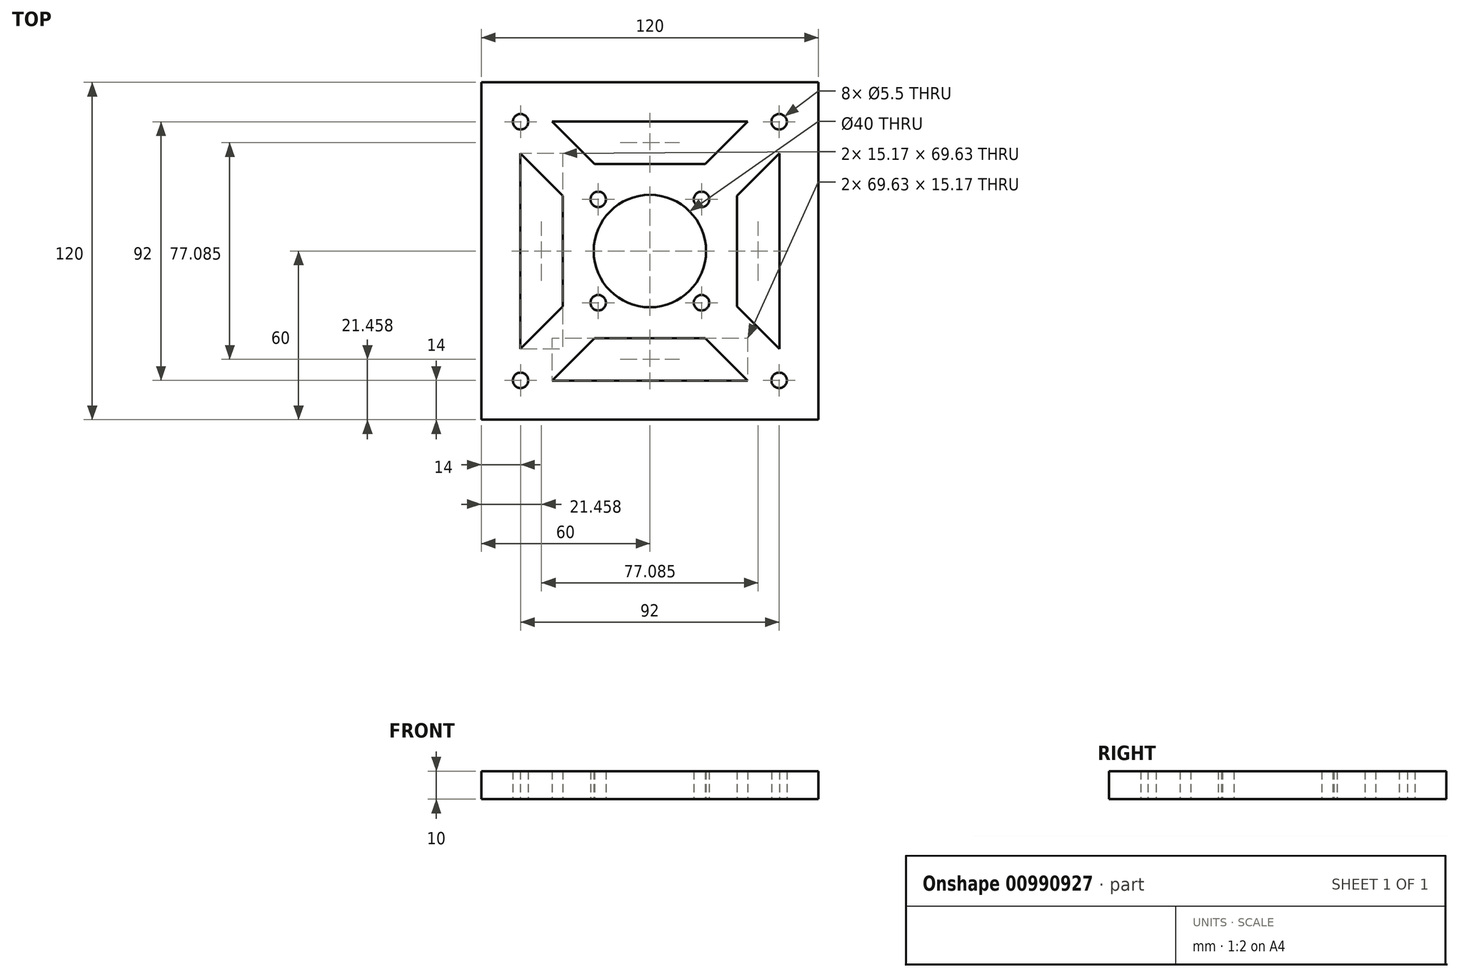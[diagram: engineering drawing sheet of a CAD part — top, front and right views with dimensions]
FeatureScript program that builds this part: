
annotation { "Feature Type Name" : "Feature", "Feature Type Description" : "" }
export const myFeature = defineFeature(function(context is Context, id is Id, definition is map)
    precondition{}
    {
        {
            var Q0;
            Q0=qCreatedBy(makeId("Top.planeOp"),FACE);
            var sketch = newSketch(context, id + "F0", { "sketchPlane" : qUnion([Q0])});
            skLineSegment(sketch, "E0.bottom", {"start": v(60, -60) * mm, "end": v(-60, -60) * mm});
            skLineSegment(sketch, "E0.top", {"start": v(60, 60) * mm, "end": v(-60, 60) * mm});
            skLineSegment(sketch, "E0.left", {"start": v(60, -60) * mm, "end": v(60, 60) * mm});
            skLineSegment(sketch, "E0.right", {"start": v(-60, -60) * mm, "end": v(-60, 60) * mm});
            skPoint(sketch, "E0.middle", {"position": v(0, 0) * mm});
            skCircle(sketch, "E1", {"center": v(0, 0) * mm, "radius": 20 * mm});
            skLineSegment(sketch, "E2", {"start": v(20, 0) * mm, "end": v(60, 0) * mm, "construction": true});
            skLineSegment(sketch, "E3", {"start": v(0, -20) * mm, "end": v(0, -60) * mm, "construction": true});
            skCircle(sketch, "E4", {"center": v(-46, 46) * mm, "radius": 2.75 * mm});
            skCircle(sketch, "E5.MirrorC", {"center": v(46, 46) * mm, "radius": 2.75 * mm});
            skCircle(sketch, "E6.MirrorC", {"center": v(-46, -46) * mm, "radius": 2.75 * mm});
            skCircle(sketch, "E7.MirrorC", {"center": v(46, -46) * mm, "radius": 2.75 * mm});
            skCircle(sketch, "E8", {"center": v(-18.38, 18.38) * mm, "radius": 2.75 * mm});
            skCircle(sketch, "E9.MirrorC", {"center": v(18.38, 18.38) * mm, "radius": 2.75 * mm});
            skCircle(sketch, "E10.MirrorC", {"center": v(-18.38, -18.38) * mm, "radius": 2.75 * mm});
            skCircle(sketch, "E11.MirrorC", {"center": v(18.38, -18.38) * mm, "radius": 2.75 * mm});
            skCircle(sketch, "E12", {"center": v(0, 0) * mm, "radius": 26 * mm, "construction": true});
            skLineSegment(sketch, "E13", {"start": v(-46, 46) * mm, "end": v(46, -46) * mm, "construction": true});
            skLineSegment(sketch, "E14", {"start": v(-46, -46) * mm, "end": v(46, 46) * mm, "construction": true});
            skLineSegment(sketch, "E15", {"start": v(-51.42, 40.11) * mm, "end": v(40.58, -51.89) * mm, "construction": true});
            skLineSegment(sketch, "E16.MirrorCS", {"start": v(-40.11, 51.42) * mm, "end": v(51.89, -40.58) * mm, "construction": true});
            skLineSegment(sketch, "E17.MirrorCS", {"start": v(40.11, 51.42) * mm, "end": v(-51.89, -40.58) * mm, "construction": true});
            skLineSegment(sketch, "E18.MirrorCS", {"start": v(51.42, 40.11) * mm, "end": v(-40.58, -51.89) * mm, "construction": true});
            skLineSegment(sketch, "E19", {"start": v(-30.96, 19.64) * mm, "end": v(-30.96, -19.64) * mm});
            skLineSegment(sketch, "E20.MirrorCS", {"start": v(19.64, -30.96) * mm, "end": v(-19.64, -30.96) * mm});
            skLineSegment(sketch, "E21.MirrorCS", {"start": v(46, -46) * mm, "end": v(-46, 46) * mm, "construction": true});
            skLineSegment(sketch, "E22.MirrorCS", {"start": v(-19.64, 30.96) * mm, "end": v(19.64, 30.96) * mm});
            skLineSegment(sketch, "E23.MirrorCS", {"start": v(30.96, 19.64) * mm, "end": v(30.96, -19.64) * mm});
            skLineSegment(sketch, "E24", {"start": v(-46.13, 34.81) * mm, "end": v(-46.13, -34.81) * mm});
            skLineSegment(sketch, "E25.MirrorCS", {"start": v(46.13, 34.81) * mm, "end": v(46.13, -34.81) * mm});
            skLineSegment(sketch, "E26.MirrorCS", {"start": v(-34.81, -46.13) * mm, "end": v(34.81, -46.13) * mm});
            skLineSegment(sketch, "E27.MirrorCS", {"start": v(-34.81, 46.13) * mm, "end": v(34.81, 46.13) * mm});
            skLineSegment(sketch, "E28", {"start": v(-46.13, 34.81) * mm, "end": v(-30.96, 19.64) * mm});
            skLineSegment(sketch, "E29", {"start": v(-30.96, -19.64) * mm, "end": v(-46.13, -34.81) * mm});
            skLineSegment(sketch, "E30", {"start": v(-34.81, -46.13) * mm, "end": v(-19.64, -30.96) * mm});
            skLineSegment(sketch, "E31", {"start": v(19.64, -30.96) * mm, "end": v(34.81, -46.13) * mm});
            skLineSegment(sketch, "E32", {"start": v(46.13, -34.81) * mm, "end": v(30.96, -19.64) * mm});
            skLineSegment(sketch, "E33", {"start": v(30.96, 19.64) * mm, "end": v(46.13, 34.81) * mm});
            skLineSegment(sketch, "E34", {"start": v(34.81, 46.13) * mm, "end": v(19.64, 30.96) * mm});
            skLineSegment(sketch, "E35", {"start": v(-19.64, 30.96) * mm, "end": v(-34.81, 46.13) * mm});
            skSolve(sketch);
        }
        {
            var Q0;
            Q0 = qSketchRegion(id + "F0", true);
            extrude(context, id + "F1", {"entities" : qUnion([Q0]), "depth" : 10 * mm, "offsetDistance" : 25 * mm});
        }
    });
